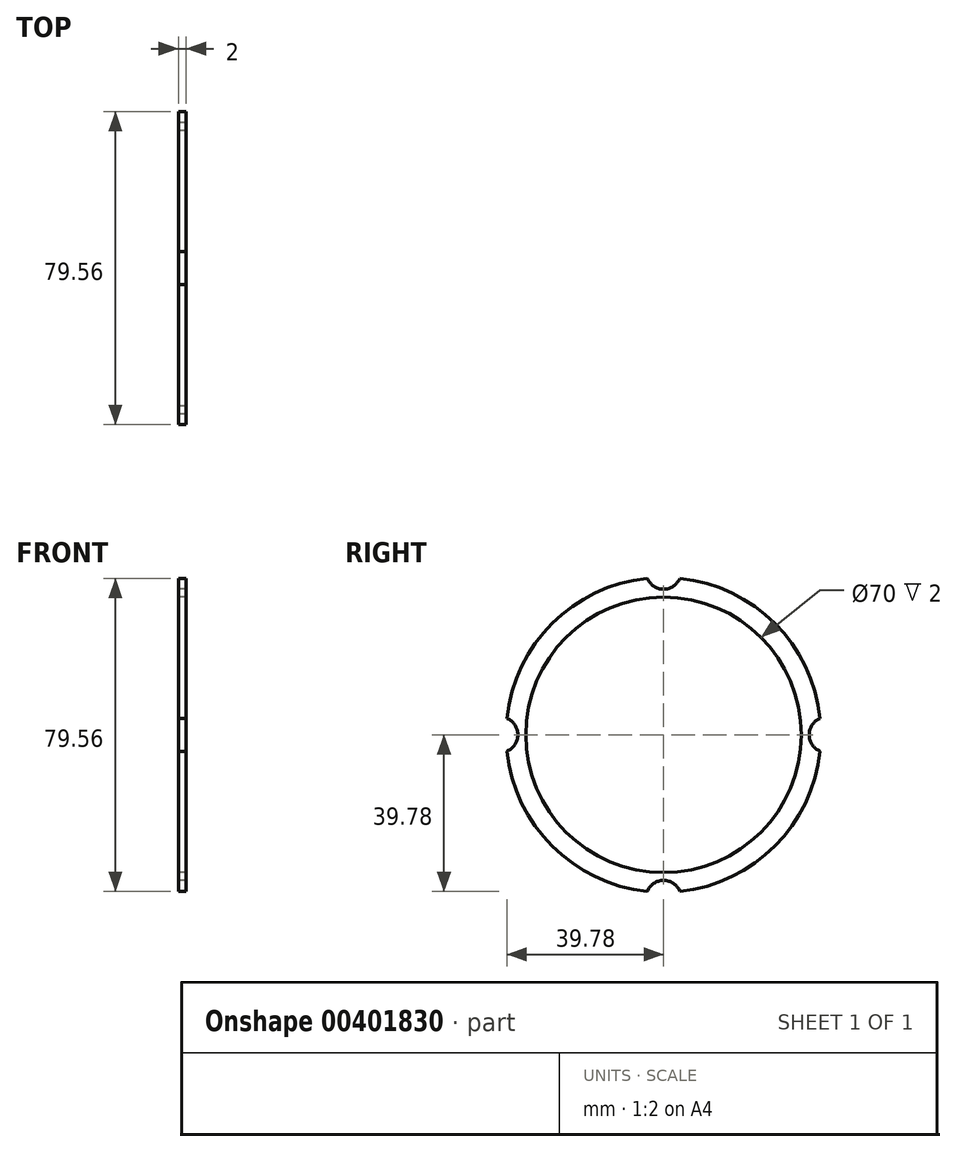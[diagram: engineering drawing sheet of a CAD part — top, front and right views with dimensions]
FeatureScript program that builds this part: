
annotation { "Feature Type Name" : "Feature", "Feature Type Description" : "" }
export const myFeature = defineFeature(function(context is Context, id is Id, definition is map)
    precondition{}
    {
        {
            var Q0;
            Q0=qCreatedBy(makeId("Right.planeOp"),FACE);
            var sketch = newSketch(context, id + "F0", { "sketchPlane" : qUnion([Q0])});
            skArc(sketch, "E0", {"start": v(-4.16, 39.78) * mm, "mid": v(-28.28, 28.28) * mm, "end": v(-39.78, 4.16) * mm});
            skCircle(sketch, "E1", {"center": v(0, 0) * mm, "radius": 35 * mm});
            skArc(sketch, "E2", {"start": v(-4.16, 39.78) * mm, "mid": v(0, 37) * mm, "end": v(4.16, 39.78) * mm});
            skArc(sketch, "E3.MirrorCS", {"start": v(-4.16, -39.78) * mm, "mid": v(0, -37) * mm, "end": v(4.16, -39.78) * mm});
            skArc(sketch, "E4.trimOffspring", {"start": v(4.16, -39.78) * mm, "mid": v(28.28, -28.28) * mm, "end": v(39.78, -4.16) * mm});
            skArc(sketch, "E5.MirrorCS", {"start": v(39.78, -4.16) * mm, "mid": v(37, 0) * mm, "end": v(39.78, 4.16) * mm});
            skArc(sketch, "E6.MirrorCS", {"start": v(-39.78, -4.16) * mm, "mid": v(-37, 0) * mm, "end": v(-39.78, 4.16) * mm});
            skArc(sketch, "E7.trimOffspring", {"start": v(-39.78, -4.16) * mm, "mid": v(-28.28, -28.28) * mm, "end": v(-4.16, -39.78) * mm});
            skArc(sketch, "E8.trimOffspring", {"start": v(39.78, 4.16) * mm, "mid": v(28.28, 28.28) * mm, "end": v(4.16, 39.78) * mm});
            skSolve(sketch);
        }
        {
            var Q0;
            Q0=makeQuery(id+"F0.imprint","IMPRINT",FACE,{"disambiguationData":[TD([[makeQuery(id+"F0.imprint","IMPRINT",EDGE,{"derivedFrom":sQuery(id+"F0.wireOp",EDGE,"E0")}),1.0]])]});
            extrude(context, id + "F1", {"entities" : qUnion([Q0]), "depth" : 2 * mm});
        }
    });
